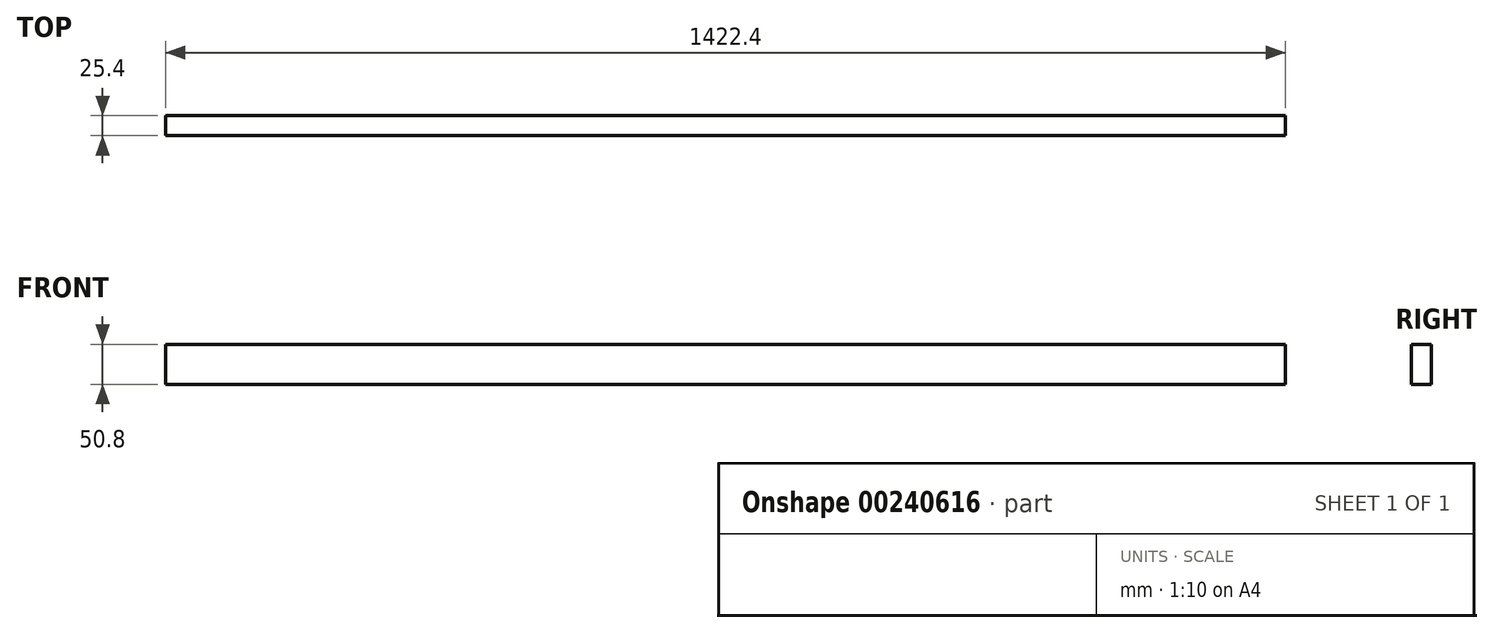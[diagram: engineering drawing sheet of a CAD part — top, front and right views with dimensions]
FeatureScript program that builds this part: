
annotation { "Feature Type Name" : "Feature", "Feature Type Description" : "" }
export const myFeature = defineFeature(function(context is Context, id is Id, definition is map)
    precondition{}
    {
        {
            var Q0;
            Q0=qCreatedBy(makeId("Right.planeOp"),FACE);
            var sketch = newSketch(context, id + "F0", { "sketchPlane" : qUnion([Q0])});
            skLineSegment(sketch, "E0.bottom", {"start": v(-12.7, 25.4) * mm, "end": v(12.7, 25.4) * mm});
            skLineSegment(sketch, "E0.top", {"start": v(-12.7, -25.4) * mm, "end": v(12.7, -25.4) * mm});
            skLineSegment(sketch, "E0.left", {"start": v(-12.7, 25.4) * mm, "end": v(-12.7, -25.4) * mm});
            skLineSegment(sketch, "E0.right", {"start": v(12.7, 25.4) * mm, "end": v(12.7, -25.4) * mm});
            skSolve(sketch);
        }
        {
            var Q0;
            Q0=makeQuery(id+"F0.imprint","IMPRINT",FACE,{"disambiguationData":[TD([[makeQuery(id+"F0.imprint","IMPRINT",EDGE,{"derivedFrom":sQuery(id+"F0.wireOp",EDGE,"E0.bottom")}),-1.0]])]});
            extrude(context, id + "F1", {"entities" : qUnion([Q0]), "endBound" : BoundingType.SYMMETRIC, "depth" : 1422.4 * mm, "offsetDistance" : 25.4 * mm});
        }
    });
